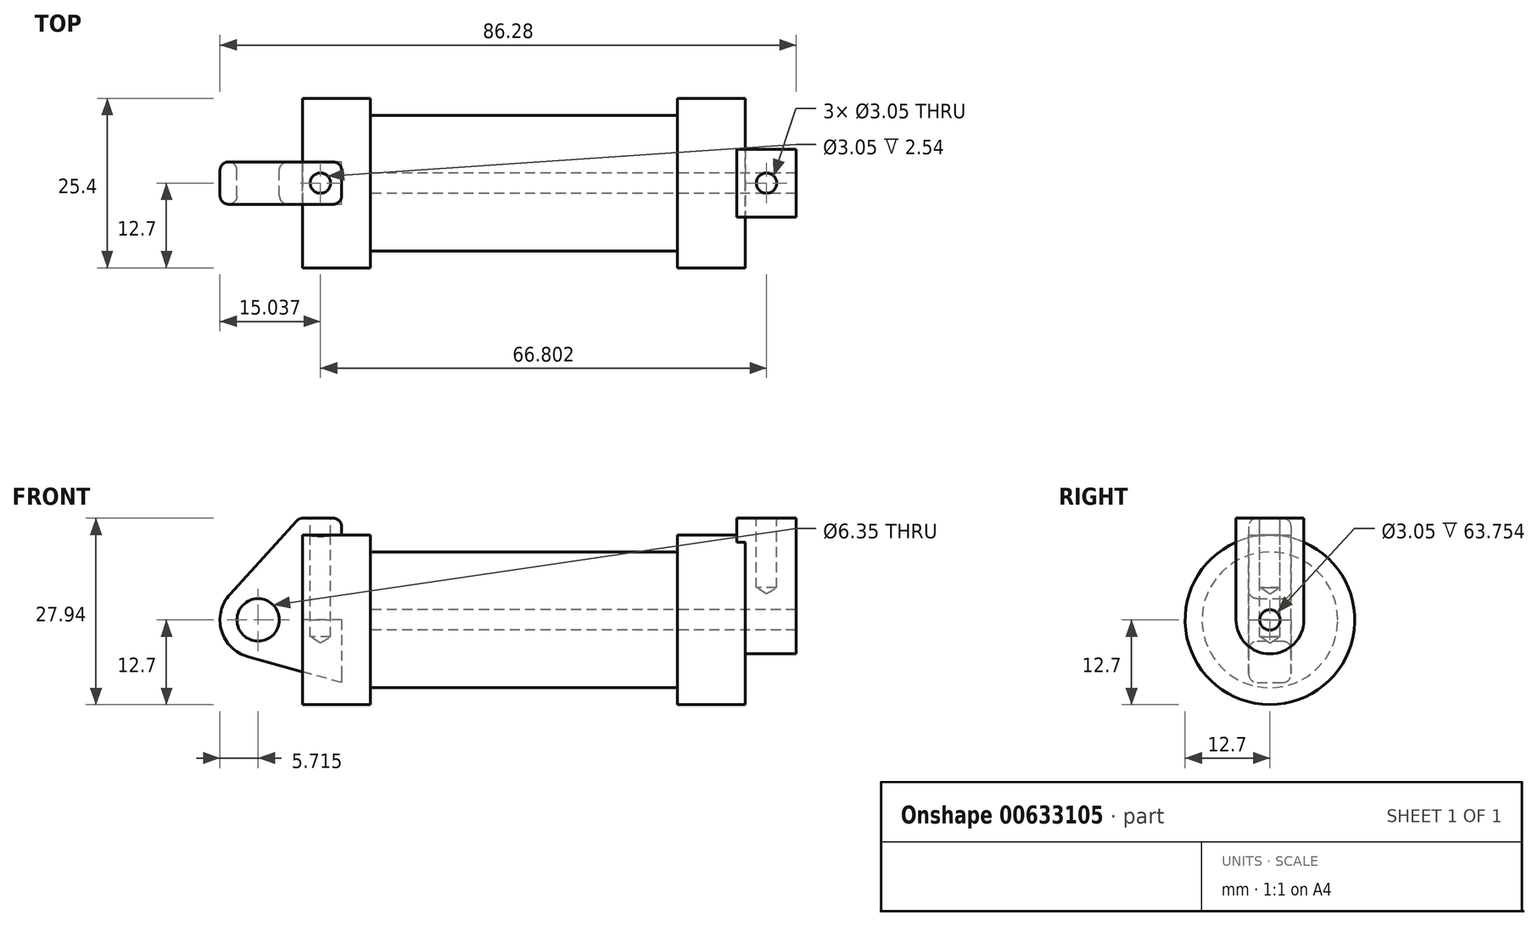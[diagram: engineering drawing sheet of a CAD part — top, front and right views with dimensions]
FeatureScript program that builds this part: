
annotation { "Feature Type Name" : "Feature", "Feature Type Description" : "" }
export const myFeature = defineFeature(function(context is Context, id is Id, definition is map)
    precondition{}
    {
        {
            var Q0;
            Q0=qCreatedBy(makeId("Front.planeOp"),FACE);
            var sketch = newSketch(context, id + "F0", { "sketchPlane" : qUnion([Q0])});
            skLineSegment(sketch, "E0", {"start": v(0, 0) * mm, "end": v(0, 12.7) * mm});
            skLineSegment(sketch, "E1", {"start": v(0, 12.7) * mm, "end": v(10.16, 12.7) * mm});
            skLineSegment(sketch, "E2", {"start": v(10.16, 12.7) * mm, "end": v(10.16, 10.16) * mm});
            skLineSegment(sketch, "E3", {"start": v(10.16, 10.16) * mm, "end": v(56.13, 10.16) * mm});
            skLineSegment(sketch, "E4", {"start": v(56.13, 10.16) * mm, "end": v(56.13, 12.7) * mm});
            skLineSegment(sketch, "E5", {"start": v(56.13, 12.7) * mm, "end": v(66.3, 12.7) * mm});
            skLineSegment(sketch, "E6", {"start": v(66.3, 12.7) * mm, "end": v(66.3, 0) * mm});
            skLineSegment(sketch, "E7", {"start": v(66.3, 0) * mm, "end": v(0, 0) * mm});
            skLineSegment(sketch, "E8", {"start": v(5.84, 15.24) * mm, "end": v(-0.5, 15.24) * mm});
            skLineSegment(sketch, "E9", {"start": v(-0.5, 15.24) * mm, "end": v(-10.88, 3.85) * mm});
            skLineSegment(sketch, "E10", {"start": v(0, 0) * mm, "end": v(-6.65, 0) * mm});
            skCircle(sketch, "E11", {"center": v(-6.65, 0) * mm, "radius": 5.72 * mm});
            skCircle(sketch, "E12", {"center": v(-6.65, 0) * mm, "radius": 3.18 * mm});
            skLineSegment(sketch, "E13", {"start": v(5.84, 15.24) * mm, "end": v(5.84, -9.4) * mm});
            skLineSegment(sketch, "E14", {"start": v(5.84, -9.4) * mm, "end": v(-8.18, -5.5) * mm});
            skSolve(sketch);
        }
        {
            var Q0;
            {var subQ0=sQuery(id+"F0.wireOp",EDGE,"E2");Q0=makeQuery(id+"F0.imprint","IMPRINT",FACE,{"disambiguationData":[TD([[makeQuery(id+"F0.imprint","IMPRINT",EDGE,{"derivedFrom":subQ0}),-1.0]])]});}
            var Q1;
            {var subQ0=sQuery(id+"F0.wireOp",EDGE,"E0");Q1=makeQuery(id+"F0.imprint","IMPRINT",FACE,{"disambiguationData":[TD([[makeQuery(id+"F0.imprint","IMPRINT",EDGE,{"derivedFrom":subQ0}),-1.0]])]});}
            var Q2;
            Q2=sQuery(id+"F0.wireOp",EDGE,"E7");
            revolve(context, id + "F1", {"entities" : qUnion([Q0, Q1]), "axis" : qUnion([Q2]), "revolveType" : RevolveType.FULL});
        }
        {
            var Q0;
            {var subQ1=sQuery(id+"F0.wireOp",EDGE,"E0");Q0=makeQuery(id+"F0.imprint","IMPRINT",FACE,{"disambiguationData":[TD([[makeQuery(id+"F0.imprint","IMPRINT",EDGE,{"derivedFrom":subQ1}),1.0]])]});}
            var Q1;
            {var subQ0=sQuery(id+"F0.wireOp",EDGE,"E14");Q1=makeQuery(id+"F0.imprint","IMPRINT",FACE,{"disambiguationData":[TD([[makeQuery(id+"F0.imprint","IMPRINT",EDGE,{"derivedFrom":subQ0}),-1.0]])]});}
            var Q2;
            {var subQ5=sQuery(id+"F0.wireOp",EDGE,"E12");Q2=makeQuery(id+"F0.imprint","IMPRINT",FACE,{"disambiguationData":[TD([[makeQuery(id+"F0.imprint","IMPRINT",EDGE,{"derivedFrom":subQ5}),-1.0]])]});}
            extrude(context, id + "F2", {"entities" : qUnion([Q0, Q1, Q2]), "endBound" : BoundingType.SYMMETRIC, "depth" : 6.35 * mm, "offsetDistance" : 25.4 * mm});
        }
        {
            var Q0;
            Q0=makeQuery(id+"F1.opRevolve","SWEPT_FACE",FACE,{"disambiguationData":[OSD([sQuery(id+"F0.wireOp",EDGE,"E6")])]});
            var sketch = newSketch(context, id + "F3", { "sketchPlane" : qUnion([Q0])});
            skCircle(sketch, "E15", {"center": v(0, 0) * mm, "radius": 1.52 * mm});
            skCircle(sketch, "E16", {"center": v(0, 0) * mm, "radius": 5.08 * mm});
            skLineSegment(sketch, "E17", {"start": v(5.08, 0) * mm, "end": v(5.08, 15.24) * mm});
            skLineSegment(sketch, "E18", {"start": v(-5.08, 0) * mm, "end": v(-5.08, 15.24) * mm});
            skLineSegment(sketch, "E19", {"start": v(-5.08, 15.24) * mm, "end": v(5.08, 15.24) * mm});
            skSolve(sketch);
        }
        {
            var Q0;
            Q0=makeQuery(id+"F3.imprint","IMPRINT",FACE,{"disambiguationData":[TD([[makeQuery(id+"F3.imprint","IMPRINT",EDGE,{"derivedFrom":sQuery(id+"F3.wireOp",EDGE,"E15")}),-1.0]])]});
            var Q1;
            {var subQ0=sQuery(id+"F3.wireOp",EDGE,"E17");var subQ1=sQuery(id+"F3.wireOp",EDGE,"E16");var subQ2=makeQuery(id+"F3.imprint","INTERSECT",VERTEX,{"derivedFrom":[subQ1,subQ0]});Q1=makeQuery(id+"F3.imprint","IMPRINT",FACE,{"disambiguationData":[TD([[makeQuery(id+"F3.imprint","IMPRINT",EDGE,{"disambiguationData":[TD([[subQ2,-1.0]])],"derivedFrom":subQ1}),-1.0]])]});}
            var Q2;
            {var subQ0=sQuery(id+"F3.wireOp",EDGE,"E19");Q2=makeQuery(id+"F3.imprint","IMPRINT",FACE,{"disambiguationData":[TD([[makeQuery(id+"F3.imprint","IMPRINT",EDGE,{"derivedFrom":subQ0}),-1.0]])]});}
            extrude(context, id + "F4", {"entities" : qUnion([Q0, Q1, Q2]), "operationType" : NewBodyOperationType.ADD, "depth" : 7.62 * mm, "offsetDistance" : 25.4 * mm, "hasSecondDirection" : true, "secondDirectionOppositeDirection" : true, "secondDirectionDepth" : 1.27 * mm});
        }
        {
            var Q0;
            Q0=makeQuery(id+"F4.boolean.opBoolean","SPLIT",FACE,{"disambiguationData":[TD([makeQuery(id+"F4.opExtrude","SWEPT_FACE",FACE,{"disambiguationData":[OSD([sQuery(id+"F3.wireOp",EDGE,"E15")])]})])],"derivedFrom":makeQuery(id+"F1.opRevolve","SWEPT_FACE",FACE,{"disambiguationData":[OSD([sQuery(id+"F0.wireOp",EDGE,"E6")])]})});
            var Q1;
            Q1=makeQuery(id+"F1.opRevolve","SWEPT_FACE",FACE,{"disambiguationData":[OSD([sQuery(id+"F0.wireOp",EDGE,"E2")])]});
            extrude(context, id + "F5", {"entities" : qUnion([Q0]), "operationType" : NewBodyOperationType.REMOVE, "endBound" : BoundingType.UP_TO_SURFACE, "oppositeDirection" : true, "depth" : 25.4 * mm, "endBoundEntityFace" : qUnion([Q1]), "offsetDistance" : 25.4 * mm});
        }
        {
            var Q0;
            Q0=makeQuery(id+"F4.opExtrude","SWEPT_FACE",FACE,{"disambiguationData":[OSD([sQuery(id+"F3.wireOp",EDGE,"E19")])]});
            var sketch = newSketch(context, id + "F6", { "sketchPlane" : qUnion([Q0])});
            skCircle(sketch, "E20", {"center": v(69.47, 0) * mm, "radius": 1.52 * mm});
            skPoint(sketch, "E20.centerSnap0", {"position": v(69.47, 5.08) * mm});
            skPoint(sketch, "E20.centerSnap1", {"position": v(73.91, 0) * mm});
            skSolve(sketch);
        }
        {
            var Q0;
            Q0=makeQuery(id+"F2.opExtrude","SWEPT_FACE",FACE,{"disambiguationData":[OSD([sQuery(id+"F0.wireOp",EDGE,"E8")])]});
            var sketch = newSketch(context, id + "F7", { "sketchPlane" : qUnion([Q0])});
            skCircle(sketch, "E21", {"center": v(2.67, 0) * mm, "radius": 1.52 * mm});
            skPoint(sketch, "E21.centerSnap0", {"position": v(5.84, 0) * mm});
            skPoint(sketch, "E21.centerSnap1", {"position": v(2.67, -3.18) * mm});
            skSolve(sketch);
        }
        {
            var Q0;
            Q0=sQuery(id+"F7.wireOp",VERTEX,"E21.center");
            var Q1;
            Q1=makeQuery(id+"F1.opRevolve","SWEPT_BODY",BODY,{"disambiguationData":[OSD([sQuery(id+"F0.wireOp",EDGE,"E0"),sQuery(id+"F0.wireOp",EDGE,"E1"),sQuery(id+"F0.wireOp",EDGE,"E2"),sQuery(id+"F0.wireOp",EDGE,"E3"),sQuery(id+"F0.wireOp",EDGE,"E4"),sQuery(id+"F0.wireOp",EDGE,"E5"),sQuery(id+"F0.wireOp",EDGE,"E6"),sQuery(id+"F0.wireOp",EDGE,"E7")])]});
            var Q2;
            Q2=makeQuery(id+"F2.opExtrude","SWEPT_BODY",BODY,{"disambiguationData":[OSD([sQuery(id+"F0.wireOp",EDGE,"E0"),sQuery(id+"F0.wireOp",EDGE,"E1"),sQuery(id+"F0.wireOp",EDGE,"E7"),sQuery(id+"F0.wireOp",EDGE,"E8"),sQuery(id+"F0.wireOp",EDGE,"E9"),sQuery(id+"F0.wireOp",EDGE,"E11"),sQuery(id+"F0.wireOp",EDGE,"E12"),sQuery(id+"F0.wireOp",EDGE,"E13"),sQuery(id+"F0.wireOp",EDGE,"E14")])]});
            hole(context, id + "F8", {"style" : HoleStyle.SIMPLE, "endStyle" : HoleEndStyle.BLIND, "holeDiameter" : 3.05 * mm, "majorDiameter" : 6.35 * mm, "holeDepth" : 17.78 * mm, "isTappedThrough" : true, "tappedDepth" : 12.7 * mm, "tapClearance" : 3, "locations" : qUnion([Q0]), "scope" : qUnion([Q1, Q2])});
        }
        {
            var Q0;
            Q0=sQuery(id+"F6.wireOp",VERTEX,"E20.center");
            var Q1;
            Q1=makeQuery(id+"F1.opRevolve","SWEPT_BODY",BODY,{"disambiguationData":[OSD([sQuery(id+"F0.wireOp",EDGE,"E0"),sQuery(id+"F0.wireOp",EDGE,"E1"),sQuery(id+"F0.wireOp",EDGE,"E2"),sQuery(id+"F0.wireOp",EDGE,"E3"),sQuery(id+"F0.wireOp",EDGE,"E4"),sQuery(id+"F0.wireOp",EDGE,"E5"),sQuery(id+"F0.wireOp",EDGE,"E6"),sQuery(id+"F0.wireOp",EDGE,"E7")])]});
            hole(context, id + "F9", {"style" : HoleStyle.SIMPLE, "endStyle" : HoleEndStyle.BLIND, "holeDiameter" : 3.05 * mm, "majorDiameter" : 6.35 * mm, "holeDepth" : 10.4 * mm, "isTappedThrough" : true, "tappedDepth" : 12.7 * mm, "tapClearance" : 3, "locations" : qUnion([Q0]), "scope" : qUnion([Q1])});
        }
        {
            var Q0;
            Q0=makeQuery(id+"F4.opExtrude","CAP_EDGE",EDGE,{"disambiguationData":[OSD([sQuery(id+"F3.wireOp",EDGE,"E19")])],"isStart":true});
            var Q1;
            Q1=makeQuery(id+"F4.opExtrude","SWEPT_EDGE",EDGE,{"disambiguationData":[OSD([sQuery(id+"F3.wireOp",EDGE,"E18"),sQuery(id+"F3.wireOp",EDGE,"E19")])]});
            var Q2;
            Q2=makeQuery(id+"F4.opExtrude","CAP_EDGE",EDGE,{"disambiguationData":[OSD([sQuery(id+"F3.wireOp",EDGE,"E19")])],"isStart":false});
            var Q3;
            Q3=makeQuery(id+"F4.opExtrude","SWEPT_EDGE",EDGE,{"disambiguationData":[OSD([sQuery(id+"F3.wireOp",EDGE,"E17"),sQuery(id+"F3.wireOp",EDGE,"E19")])]});
            var Q4;
            Q4=makeQuery(id+"F1.opRevolve","SWEPT_EDGE",EDGE,{"disambiguationData":[OSD([sQuery(id+"F0.wireOp",EDGE,"E4"),sQuery(id+"F0.wireOp",EDGE,"E5")])]});
            var Q5;
            Q5=makeQuery(id+"F4.boolean.opBoolean","INTERSECT",EDGE,{"derivedFrom":[makeQuery(id+"F1.opRevolve","SWEPT_FACE",FACE,{"disambiguationData":[OSD([sQuery(id+"F0.wireOp",EDGE,"E5")])]}),makeQuery(id+"F4.opExtrude","CAP_FACE",FACE,{"disambiguationData":[OSD([sQuery(id+"F3.wireOp",EDGE,"E15"),sQuery(id+"F3.wireOp",EDGE,"E16"),sQuery(id+"F3.wireOp",EDGE,"E17"),sQuery(id+"F3.wireOp",EDGE,"E18"),sQuery(id+"F3.wireOp",EDGE,"E19")])],"isStart":true})]});
            var Q6;
            Q6=makeQuery(id+"F4.opExtrude","CAP_EDGE",EDGE,{"disambiguationData":[OSD([sQuery(id+"F3.wireOp",EDGE,"E18")])],"isStart":true});
            var Q7;
            Q7=makeQuery(id+"F4.opExtrude","CAP_EDGE",EDGE,{"disambiguationData":[OSD([sQuery(id+"F3.wireOp",EDGE,"E17")])],"isStart":true});
            var Q8;
            Q8=makeQuery(id+"F4.opExtrude","CAP_EDGE",EDGE,{"disambiguationData":[OSD([sQuery(id+"F3.wireOp",EDGE,"E18")])],"isStart":false});
            var Q9;
            Q9=makeQuery(id+"F4.opExtrude","SWEPT_EDGE",EDGE,{"disambiguationData":[OSD([sQuery(id+"F3.wireOp",EDGE,"E16"),sQuery(id+"F3.wireOp",EDGE,"E18")])]});
            var Q10;
            Q10=makeQuery(id+"F4.opExtrude","CAP_EDGE",EDGE,{"disambiguationData":[OSD([sQuery(id+"F3.wireOp",EDGE,"E16")])],"isStart":false});
            var Q11;
            Q11=makeQuery(id+"F4.opExtrude","CAP_EDGE",EDGE,{"disambiguationData":[OSD([sQuery(id+"F3.wireOp",EDGE,"E17")])],"isStart":false});
            var Q12;
            Q12=makeQuery(id+"F1.opRevolve","SWEPT_EDGE",EDGE,{"disambiguationData":[OSD([sQuery(id+"F0.wireOp",EDGE,"E5"),sQuery(id+"F0.wireOp",EDGE,"E6")])]});
            var Q13;
            Q13=makeQuery(id+"F1.opRevolve","SWEPT_EDGE",EDGE,{"disambiguationData":[OSD([sQuery(id+"F0.wireOp",EDGE,"E0"),sQuery(id+"F0.wireOp",EDGE,"E1")])]});
            var Q14;
            Q14=makeQuery(id+"F1.opRevolve","SWEPT_EDGE",EDGE,{"disambiguationData":[OSD([sQuery(id+"F0.wireOp",EDGE,"E1"),sQuery(id+"F0.wireOp",EDGE,"E2")])]});
            var Q15;
            Q15=makeQuery(id+"F2.opExtrude","CAP_EDGE",EDGE,{"disambiguationData":[OSD([sQuery(id+"F0.wireOp",EDGE,"E8")])],"isStart":false});
            var Q16;
            Q16=makeQuery(id+"F2.opExtrude","SWEPT_EDGE",EDGE,{"disambiguationData":[OSD([sQuery(id+"F0.wireOp",EDGE,"E8"),sQuery(id+"F0.wireOp",EDGE,"E9")])]});
            var Q17;
            Q17=makeQuery(id+"F2.opExtrude","CAP_EDGE",EDGE,{"disambiguationData":[OSD([sQuery(id+"F0.wireOp",EDGE,"E8")])],"isStart":true});
            var Q18;
            Q18=makeQuery(id+"F2.opExtrude","SWEPT_EDGE",EDGE,{"disambiguationData":[OSD([sQuery(id+"F0.wireOp",EDGE,"E8"),sQuery(id+"F0.wireOp",EDGE,"E13")])]});
            var Q19;
            Q19=makeQuery(id+"F2.opExtrude","CAP_EDGE",EDGE,{"disambiguationData":[OSD([sQuery(id+"F0.wireOp",EDGE,"E12")])],"isStart":true});
            var Q20;
            Q20=makeQuery(id+"F2.opExtrude","CAP_EDGE",EDGE,{"disambiguationData":[OSD([sQuery(id+"F0.wireOp",EDGE,"E14")])],"isStart":true});
            var Q21;
            Q21=makeQuery(id+"F2.opExtrude","CAP_EDGE",EDGE,{"disambiguationData":[OSD([sQuery(id+"F0.wireOp",EDGE,"E11")])],"isStart":true});
            var Q22;
            Q22=makeQuery(id+"F2.opExtrude","CAP_EDGE",EDGE,{"disambiguationData":[OSD([sQuery(id+"F0.wireOp",EDGE,"E9")])],"isStart":true});
            var Q23;
            Q23=makeQuery(id+"F2.opExtrude","CAP_EDGE",EDGE,{"disambiguationData":[OSD([sQuery(id+"F0.wireOp",EDGE,"E14")])],"isStart":false});
            var Q24;
            Q24=makeQuery(id+"F2.opExtrude","CAP_EDGE",EDGE,{"disambiguationData":[OSD([sQuery(id+"F0.wireOp",EDGE,"E11")])],"isStart":false});
            var Q25;
            Q25=makeQuery(id+"F2.opExtrude","CAP_EDGE",EDGE,{"disambiguationData":[OSD([sQuery(id+"F0.wireOp",EDGE,"E12")])],"isStart":false});
            var Q26;
            Q26=makeQuery(id+"F2.opExtrude","CAP_EDGE",EDGE,{"disambiguationData":[OSD([sQuery(id+"F0.wireOp",EDGE,"E9")])],"isStart":false});
            var Q27;
            {var subQ0=sQuery(id+"F0.wireOp",EDGE,"E13");Q27=makeQuery(id+"F2.opExtrude","CAP_EDGE",EDGE,{"disambiguationData":[OSD([subQ0]),TDD([makeQuery(id+"F0.imprint","IMPRINT",EDGE,{"disambiguationData":[TD([[makeQuery(id+"F0.imprint","INTERSECT",VERTEX,{"derivedFrom":[sQuery(id+"F0.wireOp",EDGE,"E8"),subQ0]}),-1.0]])],"derivedFrom":subQ0})])],"isStart":true});}
            var Q28;
            {var subQ0=sQuery(id+"F0.wireOp",EDGE,"E13");Q28=makeQuery(id+"F2.opExtrude","CAP_EDGE",EDGE,{"disambiguationData":[OSD([subQ0]),TDD([makeQuery(id+"F0.imprint","IMPRINT",EDGE,{"disambiguationData":[TD([[makeQuery(id+"F0.imprint","INTERSECT",VERTEX,{"derivedFrom":[sQuery(id+"F0.wireOp",EDGE,"E8"),subQ0]}),-1.0]])],"derivedFrom":subQ0})])],"isStart":false});}
            fillet(context, id + "F10", {"entities" : qUnion([Q0, Q1, Q2, Q3, Q4, Q5, Q6, Q7, Q8, Q9, Q10, Q11, Q12, Q13, Q14, Q15, Q16, Q17, Q18, Q19, Q20, Q21, Q22, Q23, Q24, Q25, Q26, Q27, Q28]), "radius" : 1.27 * mm, "tangentPropagation" : true, "allowEdgeOverflow" : false});
        }
    });
